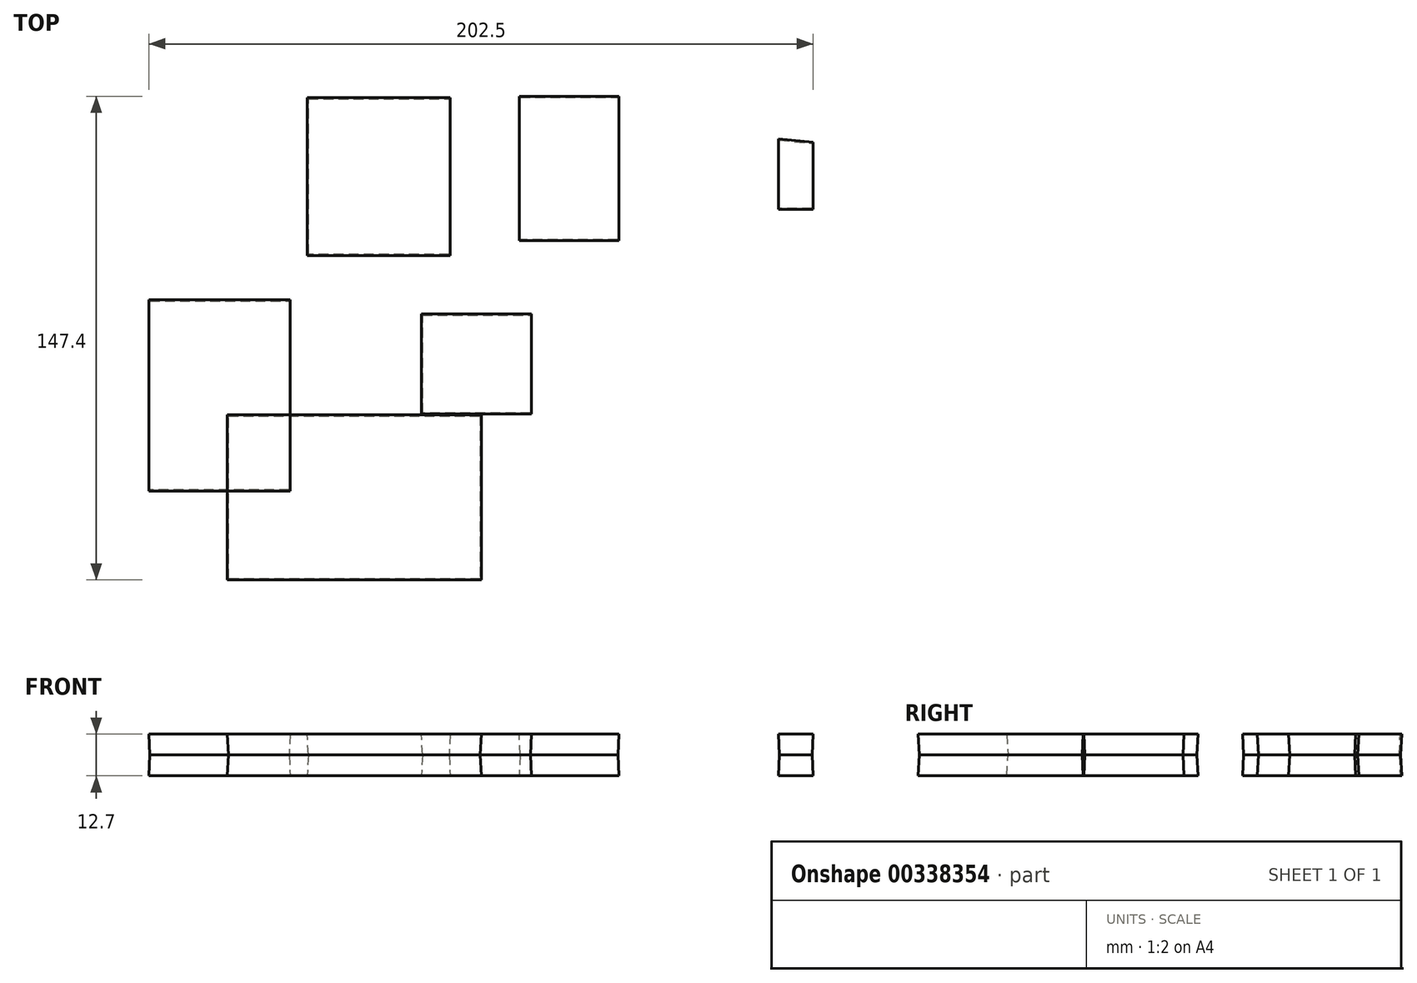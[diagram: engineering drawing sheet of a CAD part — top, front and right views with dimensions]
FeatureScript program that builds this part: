
annotation { "Feature Type Name" : "Feature", "Feature Type Description" : "" }
export const myFeature = defineFeature(function(context is Context, id is Id, definition is map)
    precondition{}
    {
        {
            var Q0;
            Q0=qCreatedBy(makeId("Top.planeOp"),FACE);
            var sketch = newSketch(context, id + "F0", { "sketchPlane" : qUnion([Q0])});
            skLineSegment(sketch, "E0.bottom", {"start": v(-98.88, -35) * mm, "end": v(-22.12, -35) * mm});
            skLineSegment(sketch, "E0.top", {"start": v(-98.88, -84.66) * mm, "end": v(-22.12, -84.66) * mm});
            skLineSegment(sketch, "E0.left", {"start": v(-98.88, -35) * mm, "end": v(-98.88, -84.66) * mm});
            skLineSegment(sketch, "E0.right", {"start": v(-22.12, -35) * mm, "end": v(-22.12, -84.66) * mm});
            skSolve(sketch);
        }
        {
            var Q0;
            Q0=qCreatedBy(makeId("Top.planeOp"),FACE);
            var sketch = newSketch(context, id + "F1", { "sketchPlane" : qUnion([Q0])});
            skFitSpline(sketch, "E1", {"points": [v(-22.58, -48.6) * mm, v(34.08, -26.63) * mm, v(44.36, -66.92) * mm, v(65.48, -54.49) * mm, v(88.98, -67.52) * mm, v(103.36, -32.22) * mm, v(125.07, -51.3) * mm, v(152.75, -25.03) * mm, v(130.54, 31.83) * mm], "startDerivative": vector(302.97, 364.51) * mm, "endDerivative": vector(-251.41, 332.1) * mm});
            skFitSpline(sketch, "E2", {"points": [v(-10.4, -85.1) * mm, v(0, -58.47) * mm, v(9.72, -41.01) * mm, v(23.45, -66.16) * mm, v(24.87, -79.97) * mm, v(52.91, -78.5) * mm, v(64.98, -71.37) * mm, v(74.94, -76.9) * mm, v(94.28, -82.7) * mm, v(113.33, -57.6) * mm, v(125.97, -79.08) * mm, v(158.87, -49.86) * mm, v(165.2, -4.3) * mm, v(143.58, 33.64) * mm], "startDerivative": vector(371.8, 24.48) * mm, "endDerivative": vector(-250.26, 389.25) * mm});
            skLineSegment(sketch, "E3.bottom", {"start": v(-39.73, -34.15) * mm, "end": v(-6.81, -34.15) * mm});
            skLineSegment(sketch, "E3.top", {"start": v(-39.73, -4.29) * mm, "end": v(-6.81, -4.29) * mm});
            skLineSegment(sketch, "E3.left", {"start": v(-39.73, -34.15) * mm, "end": v(-39.73, -4.29) * mm});
            skLineSegment(sketch, "E3.right", {"start": v(-6.81, -34.15) * mm, "end": v(-6.81, -4.29) * mm});
            skFitSpline(sketch, "E4", {"points": [v(143.58, 33.64) * mm, v(130.54, 54.86) * mm, v(102.94, 62.99) * mm, v(91.66, 75.63) * mm, v(55.54, 79.7) * mm], "startDerivative": vector(-35.17, 105.04) * mm, "endDerivative": vector(-148.18, -4.9) * mm});
            skFitSpline(sketch, "E5", {"points": [v(130.54, 31.83) * mm, v(107, 31.83) * mm, v(101.14, 43.57) * mm, v(84.43, 61.18) * mm, v(57.8, 64.8) * mm], "startDerivative": vector(-135.53, 83.03) * mm, "endDerivative": vector(-115.75, -8.4) * mm});
            skFitSpline(sketch, "E6", {"points": [v(55.54, 79.7) * mm, v(35.21, 68.85) * mm], "startDerivative": vector(-28.9, -15.35) * mm, "endDerivative": vector(2.7, -39.28) * mm});
            skFitSpline(sketch, "E7", {"points": [v(35.21, 68.85) * mm, v(35.21, 16.93) * mm, v(28.44, 5.2) * mm, v(19.86, 5.2) * mm, v(14.9, 18.74) * mm, v(9.47, 68.85) * mm, v(-5.88, 82.85) * mm, v(-25.3, 85.1) * mm, v(-32.07, 52.15) * mm, v(-31.62, 28.67) * mm, v(-43.8, 14.67) * mm, v(-74.97, 11.51) * mm, v(-75.87, 25.51) * mm, v(-76.77, 68.85) * mm, v(-99.35, 86.46) * mm, v(-128.25, 81.95) * mm, v(-137.73, 53.5) * mm, v(-143.15, -64.34) * mm, v(-141.34, -94.14) * mm, v(-83.54, -103.17) * mm, v(-30.26, -105.43) * mm, v(-10.4, -85.1) * mm], "startDerivative": vector(58.06, -974.66) * mm, "endDerivative": vector(60.47, 644.6) * mm});
            skFitSpline(sketch, "E8", {"points": [v(57.8, 64.8) * mm, v(57.8, 9.7) * mm, v(39.28, -11.06) * mm, v(0, -9.26) * mm, v(0, 30.48) * mm, v(0, 55.76) * mm, v(-13.56, 64.8) * mm, v(-14.91, 25.96) * mm, v(-10.4, 4.29) * mm, v(-54.2, -4.29) * mm, v(-84.45, -12.42) * mm, v(-98.45, 14.67) * mm, v(-95.28, 48.99) * mm, v(-105.67, 68.85) * mm, v(-119.67, 49.9) * mm, v(-121.47, 26.41) * mm, v(-121.93, -66.6) * mm, v(-99.8, -72.47) * mm, v(-98, -85.1) * mm, v(-23.04, -85.1) * mm], "startDerivative": vector(81.58, -901.53) * mm, "endDerivative": vector(1237.97, 169.5) * mm});
            skSolve(sketch);
        }
        {
            var Q0;
            Q0=qCreatedBy(makeId("Top.planeOp"),FACE);
            var sketch = newSketch(context, id + "F2", { "sketchPlane" : qUnion([Q0])});
            skLineSegment(sketch, "E9.bottom", {"start": v(69.08, 28.22) * mm, "end": v(79.01, 28.22) * mm});
            skLineSegment(sketch, "E9.top", {"start": v(69.08, 42.22) * mm, "end": v(79.01, 42.22) * mm});
            skLineSegment(sketch, "E9.left", {"start": v(69.08, 28.22) * mm, "end": v(69.08, 42.22) * mm});
            skLineSegment(sketch, "E9.right", {"start": v(79.01, 28.22) * mm, "end": v(79.01, 42.22) * mm});
            skLineSegment(sketch, "E10", {"start": v(69.08, 42.22) * mm, "end": v(69.08, 48.99) * mm});
            skLineSegment(sketch, "E11", {"start": v(79.01, 42.22) * mm, "end": v(79.01, 48.09) * mm});
            skArc(sketch, "E12", {"start": v(79.01, 48.09) * mm, "mid": v(74.54, 53.98) * mm, "end": v(69.08, 48.99) * mm});
            skLineSegment(sketch, "E13", {"start": v(69.08, 48.99) * mm, "end": v(79.01, 48.09) * mm});
            skSolve(sketch);
        }
        {
            var Q0;
            Q0=qCreatedBy(makeId("Top.planeOp"),FACE);
            var sketch = newSketch(context, id + "F3", { "sketchPlane" : qUnion([Q0])});
            skLineSegment(sketch, "E14.bottom", {"start": v(-9.94, 62.08) * mm, "end": v(19.83, 62.08) * mm});
            skLineSegment(sketch, "E14.top", {"start": v(-9.94, 18.7) * mm, "end": v(19.83, 18.7) * mm});
            skLineSegment(sketch, "E14.left", {"start": v(-9.94, 62.08) * mm, "end": v(-9.94, 18.7) * mm});
            skLineSegment(sketch, "E14.right", {"start": v(19.83, 62.08) * mm, "end": v(19.83, 18.7) * mm});
            skSolve(sketch);
        }
        {
            var Q0;
            Q0=qCreatedBy(makeId("Top.planeOp"),FACE);
            var sketch = newSketch(context, id + "F4", { "sketchPlane" : qUnion([Q0])});
            skLineSegment(sketch, "E15.bottom", {"start": v(-74.51, 61.61) * mm, "end": v(-31.62, 61.61) * mm});
            skLineSegment(sketch, "E15.top", {"start": v(-74.51, 14.2) * mm, "end": v(-31.62, 14.2) * mm});
            skLineSegment(sketch, "E15.left", {"start": v(-74.51, 61.61) * mm, "end": v(-74.51, 14.2) * mm});
            skLineSegment(sketch, "E15.right", {"start": v(-31.62, 61.61) * mm, "end": v(-31.62, 14.2) * mm});
            skSolve(sketch);
        }
        {
            var Q0;
            Q0=qCreatedBy(makeId("Top.planeOp"),FACE);
            var sketch = newSketch(context, id + "F5", { "sketchPlane" : qUnion([Q0])});
            skLineSegment(sketch, "E16.bottom", {"start": v(-122.83, 0) * mm, "end": v(-80.38, 0) * mm});
            skLineSegment(sketch, "E16.top", {"start": v(-122.83, -57.6) * mm, "end": v(-80.38, -57.6) * mm});
            skLineSegment(sketch, "E16.left", {"start": v(-122.83, 0) * mm, "end": v(-122.83, -57.6) * mm});
            skLineSegment(sketch, "E16.right", {"start": v(-80.38, 0) * mm, "end": v(-80.38, -57.6) * mm});
            skSolve(sketch);
        }
        {
            var Q0;
            Q0=makeQuery(id+"F0.imprint","IMPRINT",FACE,{"disambiguationData":[TD([[makeQuery(id+"F0.imprint","IMPRINT",EDGE,{"derivedFrom":sQuery(id+"F0.wireOp",EDGE,"E0.bottom")}),-1.0]])]});
            var Q1;
            Q1=makeQuery(id+"F5.imprint","IMPRINT",FACE,{"disambiguationData":[TD([[makeQuery(id+"F5.imprint","IMPRINT",EDGE,{"derivedFrom":sQuery(id+"F5.wireOp",EDGE,"E16.bottom")}),-1.0]])]});
            var Q2;
            Q2=makeQuery(id+"F1.imprint","IMPRINT",FACE,{"disambiguationData":[TD([[makeQuery(id+"F1.imprint","IMPRINT",EDGE,{"derivedFrom":sQuery(id+"F1.wireOp",EDGE,"E3.bottom")}),1.0]])]});
            var Q3;
            Q3=makeQuery(id+"F3.imprint","IMPRINT",FACE,{"disambiguationData":[TD([[makeQuery(id+"F3.imprint","IMPRINT",EDGE,{"derivedFrom":sQuery(id+"F3.wireOp",EDGE,"E14.bottom")}),-1.0]])]});
            var Q4;
            Q4=makeQuery(id+"F2.imprint","IMPRINT",FACE,{"disambiguationData":[TD([[makeQuery(id+"F2.imprint","IMPRINT",EDGE,{"derivedFrom":sQuery(id+"F2.wireOp",EDGE,"E9.bottom")}),1.0]])]});
            var Q5;
            Q5=makeQuery(id+"F2.imprint","IMPRINT",FACE,{"disambiguationData":[TD([[makeQuery(id+"F2.imprint","IMPRINT",EDGE,{"derivedFrom":sQuery(id+"F2.wireOp",EDGE,"E9.top")}),1.0]])]});
            var Q6;
            Q6=makeQuery(id+"F4.imprint","IMPRINT",FACE,{"disambiguationData":[TD([[makeQuery(id+"F4.imprint","IMPRINT",EDGE,{"derivedFrom":sQuery(id+"F4.wireOp",EDGE,"E15.bottom")}),-1.0]])]});
            extrude(context, id + "F6", {"entities" : qUnion([Q0, Q1, Q2, Q3, Q4, Q5, Q6]), "endBound" : BoundingType.SYMMETRIC, "depth" : 12.7 * mm, "hasDraft" : true, "draftAngle" : 3 * degree});
        }
    });
